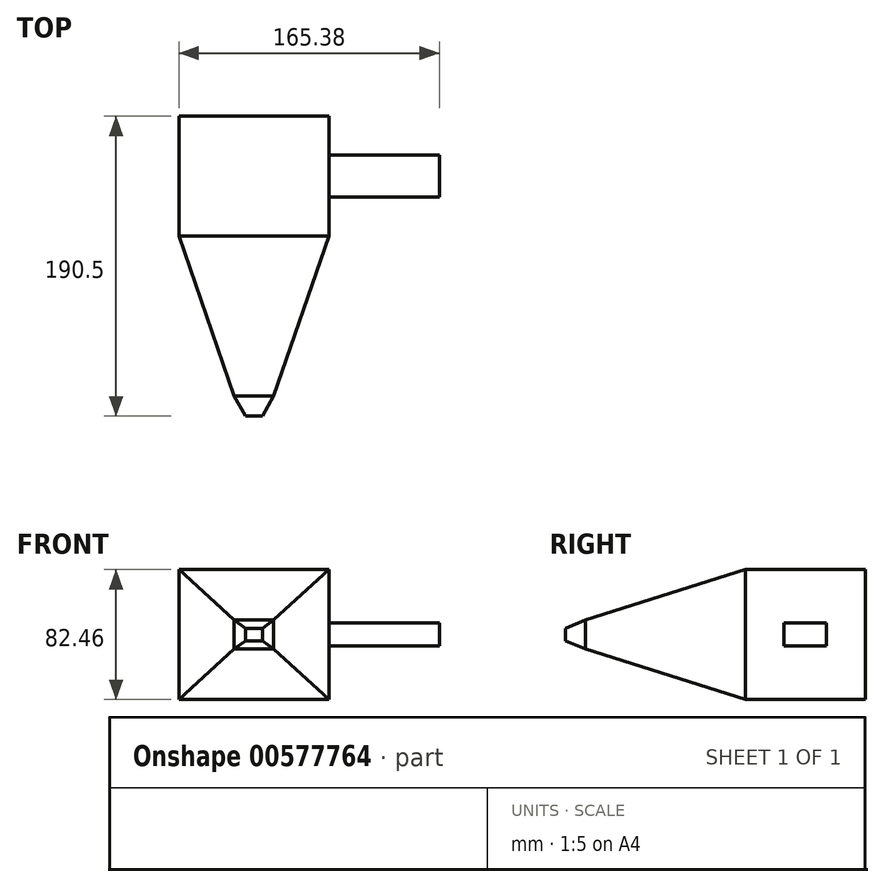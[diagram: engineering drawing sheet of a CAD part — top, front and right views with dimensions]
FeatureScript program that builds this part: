
annotation { "Feature Type Name" : "Feature", "Feature Type Description" : "" }
export const myFeature = defineFeature(function(context is Context, id is Id, definition is map)
    precondition{}
    {
        {
            var Q0;
            Q0=qCreatedBy(makeId("Front.planeOp"),FACE);
            var sketch = newSketch(context, id + "F0", { "sketchPlane" : qUnion([Q0])});
            skLineSegment(sketch, "E0.bottom", {"start": v(12.52, -9.16) * mm, "end": v(-12.52, -9.16) * mm});
            skLineSegment(sketch, "E0.top", {"start": v(12.52, 9.16) * mm, "end": v(-12.52, 9.16) * mm});
            skLineSegment(sketch, "E0.left", {"start": v(12.52, -9.16) * mm, "end": v(12.52, 9.16) * mm});
            skLineSegment(sketch, "E0.right", {"start": v(-12.52, -9.16) * mm, "end": v(-12.52, 9.16) * mm});
            skPoint(sketch, "E0.middle", {"position": v(0, 0) * mm});
            skSolve(sketch);
        }
        {
            var Q0;
            Q0=qCreatedBy(makeId("Front.planeOp"),FACE);
            cPlane(context, id + "F1", {"entities" : qUnion([Q0]), "cplaneType" : CPlaneType.OFFSET, "offset" : 101.6 * mm, "oppositeDirection" : true, "width" : 152.4 * mm, "height" : 152.4 * mm});
        }
        {
            var Q0;
            Q0=qCreatedBy(id+"F1.planeOp",FACE);
            var sketch = newSketch(context, id + "F2", { "sketchPlane" : qUnion([Q0])});
            skLineSegment(sketch, "E1.bottom", {"start": v(47.64, -41.23) * mm, "end": v(-47.64, -41.23) * mm});
            skLineSegment(sketch, "E1.top", {"start": v(47.64, 41.23) * mm, "end": v(-47.64, 41.23) * mm});
            skLineSegment(sketch, "E1.left", {"start": v(47.64, -41.23) * mm, "end": v(47.64, 41.23) * mm});
            skLineSegment(sketch, "E1.right", {"start": v(-47.64, -41.23) * mm, "end": v(-47.64, 41.23) * mm});
            skPoint(sketch, "E1.middle", {"position": v(0, 0) * mm});
            skSolve(sketch);
        }
        {
            var Q0;
            Q0=makeQuery(id+"F2.imprint","IMPRINT",FACE,{"disambiguationData":[TD([[makeQuery(id+"F2.imprint","IMPRINT",EDGE,{"derivedFrom":sQuery(id+"F2.wireOp",EDGE,"E1.bottom")}),-1.0]])]});
            var Q1;
            Q1=makeQuery(id+"F0.imprint","IMPRINT",FACE,{"disambiguationData":[TD([[makeQuery(id+"F0.imprint","IMPRINT",EDGE,{"derivedFrom":sQuery(id+"F0.wireOp",EDGE,"E0.bottom")}),-1.0]])]});
            loft(context, id + "F3", {"sheetProfilesArray" : [{ "sheetProfileEntities" : qUnion([Q0]) }, { "sheetProfileEntities" : qUnion([Q1]) }]});
        }
        {
            var Q0;
            Q0=makeQuery(id+"F3.opLoft","CAP_FACE",FACE,{"disambiguationData":[OSD([makeQuery(id+"F2.imprint","IMPRINT",FACE,{"disambiguationData":[TD([[makeQuery(id+"F2.imprint","IMPRINT",EDGE,{"derivedFrom":sQuery(id+"F2.wireOp",EDGE,"E1.bottom")}),-1.0]])]})])],"isStart":true});
            extrude(context, id + "F4", {"entities" : qUnion([Q0]), "operationType" : NewBodyOperationType.ADD, "depth" : 76.2 * mm, "offsetDistance" : 25.4 * mm});
        }
        {
            var Q0;
            Q0=makeQuery(id+"F4.opExtrude","CAP_FACE",FACE,{"disambiguationData":[OSD([makeQuery(id+"F2.imprint","IMPRINT",FACE,{"disambiguationData":[TD([[makeQuery(id+"F2.imprint","IMPRINT",EDGE,{"derivedFrom":sQuery(id+"F2.wireOp",EDGE,"E1.bottom")}),-1.0]])]})])],"isStart":false});
            var sketch = newSketch(context, id + "F5", { "sketchPlane" : qUnion([Q0])});
            skLineSegment(sketch, "E2", {"start": v(0, 41.23) * mm, "end": v(0, -41.23) * mm});
            skLineSegment(sketch, "E3", {"start": v(-47.64, 0) * mm, "end": v(0, 0) * mm});
            skLineSegment(sketch, "E4", {"start": v(0, 0) * mm, "end": v(47.64, 0) * mm});
            skLineSegment(sketch, "E5", {"start": v(0, 41.23) * mm, "end": v(47.64, 41.23) * mm});
            skLineSegment(sketch, "E6", {"start": v(47.64, 0) * mm, "end": v(47.64, 41.23) * mm});
            skCircle(sketch, "E7", {"center": v(23.82, 20.61) * mm, "radius": 7.47 * mm});
            skCircle(sketch, "E8", {"center": v(23.82, 20.61) * mm, "radius": 5.32 * mm});
            skCircle(sketch, "E9.MirrorC", {"center": v(-23.82, 20.61) * mm, "radius": 5.32 * mm});
            skCircle(sketch, "E10.MirrorC", {"center": v(-23.82, 20.61) * mm, "radius": 7.47 * mm});
            skCircle(sketch, "E11.MirrorC", {"center": v(23.82, -20.61) * mm, "radius": 7.47 * mm});
            skCircle(sketch, "E12.MirrorC", {"center": v(23.82, -20.61) * mm, "radius": 5.32 * mm});
            skCircle(sketch, "E13.MirrorC", {"center": v(-23.82, -20.61) * mm, "radius": 7.47 * mm});
            skCircle(sketch, "E14.MirrorC", {"center": v(-23.82, -20.61) * mm, "radius": 5.32 * mm});
            skSolve(sketch);
        }
        {
            var Q0;
            Q0=qCreatedBy(id+"F1.planeOp",FACE);
            cPlane(context, id + "F6", {"entities" : qUnion([Q0]), "cplaneType" : CPlaneType.OFFSET, "offset" : 129.29 * mm, "oppositeDirection" : true, "width" : 152.4 * mm, "height" : 152.4 * mm});
        }
        {
            var Q0;
            Q0=qCreatedBy(id+"F6.planeOp",FACE);
            var sketch = newSketch(context, id + "F7", { "sketchPlane" : qUnion([Q0])});
            skCircle(sketch, "E15.MirrorC", {"center": v(23.82, 20.61) * mm, "radius": 20 * mm});
            skLineSegment(sketch, "E16", {"start": v(0, 0) * mm, "end": v(-7.63, 0) * mm});
            skCircle(sketch, "E17.MirrorC", {"center": v(-23.82, 20.61) * mm, "radius": 20 * mm});
            skCircle(sketch, "E18.MirrorC", {"center": v(23.82, -20.61) * mm, "radius": 20 * mm});
            skCircle(sketch, "E19.MirrorC", {"center": v(-23.82, -20.61) * mm, "radius": 20 * mm});
            skSolve(sketch);
        }
        {
            var Q0;
            Q0=makeQuery(id+"F7.imprint","IMPRINT",FACE,{"disambiguationData":[TD([[makeQuery(id+"F7.imprint","IMPRINT",EDGE,{"derivedFrom":sQuery(id+"F7.wireOp",EDGE,"nVTYODjv-nGzI-6jeX-yUVM-1MBAlKGWY7QA")}),1.0]])]});
            var Q1;
            Q1=makeQuery(id+"F5.imprint","IMPRINT",FACE,{"disambiguationData":[TD([[makeQuery(id+"F5.imprint","IMPRINT",EDGE,{"derivedFrom":sQuery(id+"F5.wireOp",EDGE,"E7")}),1.0]])]});
            var Q2;
            Q2=makeQuery(id+"F7.imprint","IMPRINT",FACE,{"disambiguationData":[TD([[makeQuery(id+"F7.imprint","IMPRINT",EDGE,{"derivedFrom":sQuery(id+"F7.wireOp",EDGE,"N5KnDaBH-QaJH-ZLX1-PXgQ-UmKpg9lYpJOV")}),1.0]])]});
            var Q3;
            Q3=sQuery(id+"F7.wireOp",EDGE,"E17.MirrorC");
            var Q4;
            Q4=sQuery(id+"F5.wireOp",EDGE,"E7");
            loft(context, id + "F8", {"bodyType" : ToolBodyType.SURFACE, "sheetProfilesArray" : [{ "sheetProfileEntities" : qUnion([Q0]) }, { "sheetProfileEntities" : qUnion([Q1]) }, { "sheetProfileEntities" : qUnion([Q2]) }], "wireProfilesArray" : [{ "wireProfileEntities" : qUnion([Q3]) }, { "wireProfileEntities" : qUnion([Q4]) }]});
        }
        {
            var Q0;
            Q0=sQuery(id+"F7.wireOp",EDGE,"E18.MirrorC");
            var Q1;
            Q1=sQuery(id+"F5.wireOp",EDGE,"E13.MirrorC");
            loft(context, id + "F9", {"bodyType" : ToolBodyType.SURFACE, "wireProfilesArray" : [{ "wireProfileEntities" : qUnion([Q0]) }, { "wireProfileEntities" : qUnion([Q1]) }]});
        }
        {
            var Q0;
            Q0=sQuery(id+"F7.wireOp",EDGE,"E15.MirrorC");
            var Q1;
            Q1=sQuery(id+"F5.wireOp",EDGE,"E10.MirrorC");
            loft(context, id + "F10", {"bodyType" : ToolBodyType.SURFACE, "wireProfilesArray" : [{ "wireProfileEntities" : qUnion([Q0]) }, { "wireProfileEntities" : qUnion([Q1]) }]});
        }
        {
            var Q0;
            Q0=makeQuery(id+"F7.imprint","IMPRINT",FACE,{"disambiguationData":[TD([[makeQuery(id+"F7.imprint","IMPRINT",EDGE,{"derivedFrom":sQuery(id+"F7.wireOp",EDGE,"13379d10-b1e6-4bb1-89e5-14711c47a1b60.MirrorC")}),-1.0]])]});
            var Q1;
            Q1=sQuery(id+"F5.wireOp",EDGE,"E11.MirrorC");
            var Q2;
            Q2=sQuery(id+"F7.wireOp",EDGE,"E19.MirrorC");
            loft(context, id + "F11", {"bodyType" : ToolBodyType.SURFACE, "sheetProfilesArray" : [{ "sheetProfileEntities" : qUnion([Q0]) }], "wireProfilesArray" : [{ "wireProfileEntities" : qUnion([Q1]) }, { "wireProfileEntities" : qUnion([Q2]) }]});
        }
        {
            var Q0;
            Q0=qCreatedBy(makeId("Front.planeOp"),FACE);
            cPlane(context, id + "F12", {"entities" : qUnion([Q0]), "cplaneType" : CPlaneType.OFFSET, "offset" : 12.7 * mm, "width" : 152.4 * mm, "height" : 152.4 * mm});
        }
        {
            var Q0;
            Q0=qCreatedBy(id+"F12.planeOp",FACE);
            var sketch = newSketch(context, id + "F13", { "sketchPlane" : qUnion([Q0])});
            skLineSegment(sketch, "E20.bottom", {"start": v(5.5, -3.97) * mm, "end": v(-5.5, -3.97) * mm});
            skLineSegment(sketch, "E20.top", {"start": v(5.5, 3.97) * mm, "end": v(-5.5, 3.97) * mm});
            skLineSegment(sketch, "E20.left", {"start": v(5.5, -3.97) * mm, "end": v(5.5, 3.97) * mm});
            skLineSegment(sketch, "E20.right", {"start": v(-5.5, -3.97) * mm, "end": v(-5.5, 3.97) * mm});
            skPoint(sketch, "E20.middle", {"position": v(0, 0) * mm});
            skSolve(sketch);
        }
        {
            var Q1;
            Q1=makeQuery(id+"F13.imprint","IMPRINT",FACE,{"disambiguationData":[TD([[makeQuery(id+"F13.imprint","IMPRINT",EDGE,{"derivedFrom":sQuery(id+"F13.wireOp",EDGE,"E20.bottom")}),-1.0]])]});
            var Q2;
            Q2=makeQuery(id+"F3.opLoft","CAP_FACE",FACE,{"disambiguationData":[OSD([makeQuery(id+"F0.imprint","IMPRINT",FACE,{"disambiguationData":[TD([[makeQuery(id+"F0.imprint","IMPRINT",EDGE,{"derivedFrom":sQuery(id+"F0.wireOp",EDGE,"E0.bottom")}),-1.0]])]})])],"isStart":true});
            loft(context, id + "F14", {"operationType" : NewBodyOperationType.ADD, "sheetProfilesArray" : [{ "sheetProfileEntities" : qUnion([Q1]) }, { "sheetProfileEntities" : qUnion([Q2]) }]});
        }
        {
            var Q0;
            Q0=makeQuery(id+"F4.opExtrude","SWEPT_FACE",FACE,{"disambiguationData":[OSD([sQuery(id+"F2.wireOp",EDGE,"E1.bottom"),sQuery(id+"F2.wireOp",EDGE,"E1.top"),sQuery(id+"F2.wireOp",EDGE,"E1.left")])]});
            var sketch = newSketch(context, id + "F15", { "sketchPlane" : qUnion([Q0])});
            skLineSegment(sketch, "E21", {"start": v(139.7, 41.23) * mm, "end": v(139.7, -41.23) * mm});
            skLineSegment(sketch, "E22", {"start": v(101.6, 0) * mm, "end": v(139.7, 0) * mm});
            skLineSegment(sketch, "E23", {"start": v(139.7, 0) * mm, "end": v(177.8, 0) * mm});
            skLineSegment(sketch, "E24.bottom", {"start": v(153.12, -7.34) * mm, "end": v(126.28, -7.34) * mm});
            skLineSegment(sketch, "E24.top", {"start": v(153.12, 7.34) * mm, "end": v(126.28, 7.34) * mm});
            skLineSegment(sketch, "E24.left", {"start": v(153.12, -7.34) * mm, "end": v(153.12, 7.34) * mm});
            skLineSegment(sketch, "E24.right", {"start": v(126.28, -7.34) * mm, "end": v(126.28, 7.34) * mm});
            skPoint(sketch, "E24.middle", {"position": v(139.7, 0) * mm});
            skSolve(sketch);
        }
        {
            var Q0;
            {var subQ3=sQuery(id+"F15.wireOp",EDGE,"E24.bottom");var subQ5=sQuery(id+"F15.wireOp",EDGE,"E24.right");var subQ7=makeQuery(id+"F15.imprint","INTERSECT",VERTEX,{"derivedFrom":[subQ3,subQ5]});Q0=makeQuery(id+"F15.imprint","IMPRINT",FACE,{"disambiguationData":[TD([[makeQuery(id+"F15.imprint","IMPRINT",EDGE,{"disambiguationData":[TD([[subQ7,1.0]])],"derivedFrom":subQ3}),-1.0]])]});}
            var Q1;
            {var subQ3=sQuery(id+"F15.wireOp",EDGE,"E24.top");var subQ5=sQuery(id+"F15.wireOp",EDGE,"E24.right");var subQ6=makeQuery(id+"F15.imprint","INTERSECT",VERTEX,{"derivedFrom":[subQ3,subQ5]});Q1=makeQuery(id+"F15.imprint","IMPRINT",FACE,{"disambiguationData":[TD([[makeQuery(id+"F15.imprint","IMPRINT",EDGE,{"disambiguationData":[TD([[subQ6,1.0]])],"derivedFrom":subQ3}),1.0]])]});}
            var Q2;
            {var subQ3=sQuery(id+"F15.wireOp",EDGE,"E24.top");var subQ5=sQuery(id+"F15.wireOp",EDGE,"E24.left");var subQ7=makeQuery(id+"F15.imprint","INTERSECT",VERTEX,{"derivedFrom":[subQ3,subQ5]});Q2=makeQuery(id+"F15.imprint","IMPRINT",FACE,{"disambiguationData":[TD([[makeQuery(id+"F15.imprint","IMPRINT",EDGE,{"disambiguationData":[TD([[subQ7,-1.0]])],"derivedFrom":subQ3}),1.0]])]});}
            var Q3;
            {var subQ3=sQuery(id+"F15.wireOp",EDGE,"E24.bottom");var subQ5=sQuery(id+"F15.wireOp",EDGE,"E24.left");var subQ6=makeQuery(id+"F15.imprint","INTERSECT",VERTEX,{"derivedFrom":[subQ3,subQ5]});Q3=makeQuery(id+"F15.imprint","IMPRINT",FACE,{"disambiguationData":[TD([[makeQuery(id+"F15.imprint","IMPRINT",EDGE,{"disambiguationData":[TD([[subQ6,-1.0]])],"derivedFrom":subQ3}),-1.0]])]});}
            extrude(context, id + "F16", {"entities" : qUnion([Q0, Q1, Q2, Q3]), "operationType" : NewBodyOperationType.ADD, "depth" : 70.1 * mm, "offsetDistance" : 25.4 * mm});
        }
    });
